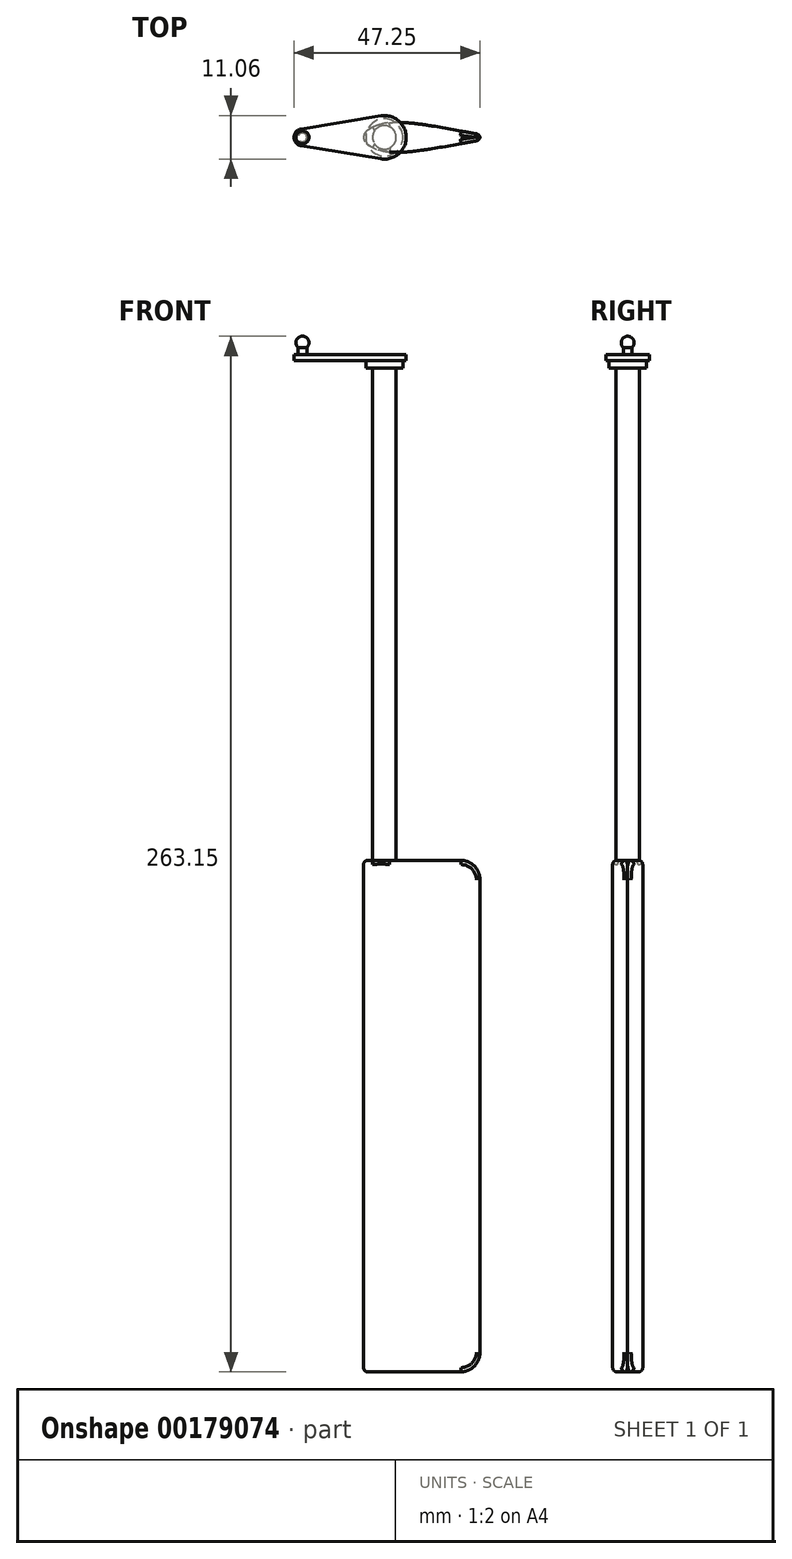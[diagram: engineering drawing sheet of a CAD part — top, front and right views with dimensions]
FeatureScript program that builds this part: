
annotation { "Feature Type Name" : "Feature", "Feature Type Description" : "" }
export const myFeature = defineFeature(function(context is Context, id is Id, definition is map)
    precondition{}
    {
        {
            var Q0;
            Q0=qCreatedBy(makeId("Top.planeOp"),FACE);
            var sketch = newSketch(context, id + "F0", { "sketchPlane" : qUnion([Q0])});
            skCircle(sketch, "E0", {"center": v(0, 0) * mm, "radius": 3 * mm});
            skSolve(sketch);
        }
        {
            var Q0;
            Q0=makeQuery(id+"F0.imprint","IMPRINT",FACE,{"disambiguationData":[TD([[makeQuery(id+"F0.imprint","IMPRINT",EDGE,{"derivedFrom":sQuery(id+"F0.wireOp",EDGE,"E0")}),1.0]])]});
            extrude(context, id + "F1", {"entities" : qUnion([Q0]), "depth" : 125 * mm});
        }
        {
            var Q0;
            Q0=makeQuery(id+"F1.opExtrude","CAP_FACE",FACE,{"disambiguationData":[OSD([sQuery(id+"F0.wireOp",EDGE,"E0")])],"isStart":false});
            var sketch = newSketch(context, id + "F2", { "sketchPlane" : qUnion([Q0])});
            skCircle(sketch, "E1", {"center": v(0, 0) * mm, "radius": 4.7 * mm});
            skSolve(sketch);
        }
        {
            var Q0;
            Q0=makeQuery(id+"F2.imprint","IMPRINT",FACE,{"disambiguationData":[TD([[makeQuery(id+"F2.imprint","IMPRINT",EDGE,{"derivedFrom":sQuery(id+"F2.wireOp",EDGE,"E1")}),1.0]])]});
            var Q1;
            Q1=makeQuery(id+"F2.imprint","IMPRINT",FACE,{"disambiguationData":[TD([[makeQuery(id+"F2.imprint","IMPRINT",EDGE,{"derivedFrom":makeQuery(id+"F1.opExtrude","CAP_EDGE",EDGE,{"disambiguationData":[OSD([sQuery(id+"F0.wireOp",EDGE,"E0")])],"isStart":false})}),1.0]])]});
            extrude(context, id + "F3", {"entities" : qUnion([Q0, Q1]), "operationType" : NewBodyOperationType.ADD, "depth" : 2 * mm});
        }
        {
            var Q0;
            Q0=makeQuery(id+"F3.opExtrude","CAP_FACE",FACE,{"disambiguationData":[OSD([sQuery(id+"F2.wireOp",EDGE,"E1")])],"isStart":false});
            var sketch = newSketch(context, id + "F4", { "sketchPlane" : qUnion([Q0])});
            skArc(sketch, "E2", {"start": v(-0.9, -5.46) * mm, "mid": v(5.53, 0) * mm, "end": v(-0.9, 5.46) * mm});
            skLineSegment(sketch, "E3", {"start": v(0, 0) * mm, "end": v(-20.81, 0) * mm});
            skArc(sketch, "E4", {"start": v(-21.16, 2.12) * mm, "mid": v(-22.97, 0) * mm, "end": v(-21.16, -2.12) * mm});
            skLineSegment(sketch, "E5", {"start": v(-21.16, 2.12) * mm, "end": v(-0.9, 5.46) * mm});
            skLineSegment(sketch, "E6", {"start": v(-21.16, -2.12) * mm, "end": v(-0.9, -5.46) * mm});
            skSolve(sketch);
        }
        {
            var Q0;
            Q0=makeQuery(id+"F4.imprint","IMPRINT",FACE,{"disambiguationData":[TD([[makeQuery(id+"F4.imprint","IMPRINT",EDGE,{"derivedFrom":sQuery(id+"F4.wireOp",EDGE,"E2")}),1.0]])]});
            var Q1;
            Q1=makeQuery(id+"F4.imprint","IMPRINT",FACE,{"disambiguationData":[TD([[makeQuery(id+"F4.imprint","IMPRINT",EDGE,{"derivedFrom":makeQuery(id+"F3.opExtrude","CAP_EDGE",EDGE,{"disambiguationData":[OSD([sQuery(id+"F2.wireOp",EDGE,"E1")])],"isStart":false})}),1.0]])]});
            extrude(context, id + "F5", {"entities" : qUnion([Q0, Q1]), "operationType" : NewBodyOperationType.ADD, "depth" : 1.5 * mm});
        }
        {
            var Q0;
            Q0=makeQuery(id+"F5.opExtrude","CAP_FACE",FACE,{"disambiguationData":[OSD([sQuery(id+"F4.wireOp",EDGE,"E2"),sQuery(id+"F4.wireOp",EDGE,"E4"),sQuery(id+"F4.wireOp",EDGE,"E5"),sQuery(id+"F4.wireOp",EDGE,"E6")])],"isStart":false});
            var sketch = newSketch(context, id + "F6", { "sketchPlane" : qUnion([Q0])});
            skCircle(sketch, "E7", {"center": v(-20.81, 0) * mm, "radius": 1.1 * mm});
            skSolve(sketch);
        }
        {
            var Q0;
            Q0=makeQuery(id+"F6.imprint","IMPRINT",FACE,{"disambiguationData":[TD([[makeQuery(id+"F6.imprint","IMPRINT",EDGE,{"derivedFrom":sQuery(id+"F6.wireOp",EDGE,"E7")}),1.0]])]});
            extrude(context, id + "F7", {"entities" : qUnion([Q0]), "operationType" : NewBodyOperationType.ADD, "depth" : 3 * mm});
        }
        {
            var Q0;
            Q0=makeQuery(id+"F7.opExtrude","CAP_FACE",FACE,{"disambiguationData":[OSD([sQuery(id+"F6.wireOp",EDGE,"E7")])],"isStart":false});
            var sketch = newSketch(context, id + "F8", { "sketchPlane" : qUnion([Q0])});
            skLineSegment(sketch, "E8", {"start": v(-19.17, 0) * mm, "end": v(-22.46, 0) * mm});
            skArc(sketch, "E9", {"start": v(-19.17, 0) * mm, "mid": v(-20.81, 1.65) * mm, "end": v(-22.46, 0) * mm});
            skSolve(sketch);
        }
        {
            var Q0;
            {var subQ0=sQuery(id+"F8.wireOp",EDGE,"E9");Q0=makeQuery(id+"F8.imprint","IMPRINT",FACE,{"disambiguationData":[TD([[makeQuery(id+"F8.imprint","IMPRINT",EDGE,{"derivedFrom":subQ0}),1.0]])]});}
            var Q1;
            {var subQ0=sQuery(id+"F8.wireOp",EDGE,"E8");var subQ1=makeQuery(id+"F7.opExtrude","CAP_EDGE",EDGE,{"disambiguationData":[OSD([sQuery(id+"F6.wireOp",EDGE,"E7")])],"isStart":false});var subQ2=makeQuery(id+"F8.imprint","INTERSECT",VERTEX,{"disambiguationData":[OD(0.0)],"derivedFrom":[subQ1,subQ0]});Q1=makeQuery(id+"F8.imprint","IMPRINT",FACE,{"disambiguationData":[TD([[makeQuery(id+"F8.imprint","IMPRINT",EDGE,{"disambiguationData":[TD([[subQ2,-1.0]])],"derivedFrom":subQ0}),-1.0]])]});}
            var Q2;
            Q2=sQuery(id+"F8.wireOp",EDGE,"E8");
            revolve(context, id + "F9", {"operationType" : NewBodyOperationType.ADD, "entities" : qUnion([Q0, Q1]), "axis" : qUnion([Q2]), "revolveType" : RevolveType.FULL});
        }
        {
            var Q0;
            Q0=makeQuery(id+"F1.opExtrude","CAP_FACE",FACE,{"disambiguationData":[OSD([sQuery(id+"F0.wireOp",EDGE,"E0")])],"isStart":true});
            var sketch = newSketch(context, id + "F10", { "sketchPlane" : qUnion([Q0])});
            skArc(sketch, "E10", {"start": v(3.2, 0) * mm, "mid": v(-1.05, 3.02) * mm, "end": v(-2.51, -1.98) * mm});
            skLineSegment(sketch, "E11", {"start": v(0, 0) * mm, "end": v(24.3, 0) * mm});
            skLineSegment(sketch, "E12", {"start": v(24.3, 0) * mm, "end": v(24.3, 0.73) * mm});
            skLineSegment(sketch, "E13", {"start": v(0, 0) * mm, "end": v(-3.2, 0) * mm});
            skArc(sketch, "E14", {"start": v(-4.54, 1.6) * mm, "mid": v(-5.29, 0) * mm, "end": v(-4.54, -1.6) * mm});
            skFitSpline(sketch, "E15", {"points": [v(24.3, 0.73) * mm, v(2.93, 3.82) * mm, v(-4.54, 1.6) * mm], "startDerivative": vector(-36.88, 6.17) * mm, "endDerivative": vector(-13.95, -11.75) * mm});
            skFitSpline(sketch, "E16.MirrorCS", {"points": [v(24.3, -0.73) * mm, v(2.93, -3.82) * mm, v(-4.54, -1.6) * mm], "startDerivative": vector(-36.88, -6.17) * mm, "endDerivative": vector(-13.95, 11.75) * mm});
            skLineSegment(sketch, "E17.MirrorCS", {"start": v(24.3, 0) * mm, "end": v(24.3, -0.73) * mm});
            skArc(sketch, "E18.trimOffspring", {"start": v(-2.51, -1.98) * mm, "mid": v(-1.1, 0) * mm, "end": v(-2.51, 1.98) * mm});
            skSolve(sketch);
        }
        {
            var Q0;
            Q0=makeQuery(id+"F10.imprint","IMPRINT",FACE,{"disambiguationData":[TD([[makeQuery(id+"F10.imprint","IMPRINT",EDGE,{"derivedFrom":sQuery(id+"F10.wireOp",EDGE,"E12")}),1.0]])]});
            var Q1;
            {var subQ0=sQuery(id+"F10.wireOp",EDGE,"E13");var subQ1=sQuery(id+"F10.wireOp",EDGE,"E11");var subQ2=makeQuery(id+"F10.imprint","INTERSECT",VERTEX,{"derivedFrom":[subQ1,subQ0]});Q1=makeQuery(id+"F10.imprint","IMPRINT",FACE,{"disambiguationData":[TD([[makeQuery(id+"F10.imprint","IMPRINT",EDGE,{"disambiguationData":[TD([[subQ2,-1.0]])],"derivedFrom":subQ1}),1.0]])]});}
            var Q2;
            {var subQ0=sQuery(id+"F10.wireOp",EDGE,"E13");var subQ1=sQuery(id+"F10.wireOp",EDGE,"E11");var subQ2=makeQuery(id+"F10.imprint","INTERSECT",VERTEX,{"derivedFrom":[subQ1,subQ0]});Q2=makeQuery(id+"F10.imprint","IMPRINT",FACE,{"disambiguationData":[TD([[makeQuery(id+"F10.imprint","IMPRINT",EDGE,{"disambiguationData":[TD([[subQ2,-1.0]])],"derivedFrom":subQ1}),-1.0]])]});}
            var Q3;
            {var subQ0=sQuery(id+"F10.wireOp",EDGE,"E18.trimOffspring");var subQ1=sQuery(id+"F10.wireOp",EDGE,"E13");var subQ2=makeQuery(id+"F10.imprint","INTERSECT",VERTEX,{"derivedFrom":[subQ1,subQ0]});Q3=makeQuery(id+"F10.imprint","IMPRINT",FACE,{"disambiguationData":[TD([[makeQuery(id+"F10.imprint","IMPRINT",EDGE,{"disambiguationData":[TD([[subQ2,-1.0]])],"derivedFrom":subQ1}),1.0]])]});}
            var Q4;
            {var subQ0=sQuery(id+"F10.wireOp",EDGE,"E18.trimOffspring");var subQ1=sQuery(id+"F10.wireOp",EDGE,"E13");var subQ2=makeQuery(id+"F10.imprint","INTERSECT",VERTEX,{"derivedFrom":[subQ1,subQ0]});Q4=makeQuery(id+"F10.imprint","IMPRINT",FACE,{"disambiguationData":[TD([[makeQuery(id+"F10.imprint","IMPRINT",EDGE,{"disambiguationData":[TD([[subQ2,-1.0]])],"derivedFrom":subQ1}),-1.0]])]});}
            var Q5;
            {var subQ0=sQuery(id+"F10.wireOp",EDGE,"E11");var subQ1=sQuery(id+"F10.wireOp",EDGE,"E10");var subQ2=makeQuery(id+"F10.imprint","INTERSECT",VERTEX,{"derivedFrom":[subQ1,subQ0]});Q5=makeQuery(id+"F10.imprint","IMPRINT",FACE,{"disambiguationData":[TD([[makeQuery(id+"F10.imprint","IMPRINT",EDGE,{"disambiguationData":[TD([[subQ2,-1.0]])],"derivedFrom":subQ1}),1.0]])]});}
            var Q6;
            {var subQ0=sQuery(id+"F10.wireOp",EDGE,"E13");var subQ1=sQuery(id+"F10.wireOp",EDGE,"E10");var subQ2=makeQuery(id+"F10.imprint","INTERSECT",VERTEX,{"derivedFrom":[subQ1,subQ0]});Q6=makeQuery(id+"F10.imprint","IMPRINT",FACE,{"disambiguationData":[TD([[makeQuery(id+"F10.imprint","IMPRINT",EDGE,{"disambiguationData":[TD([[subQ2,1.0]])],"derivedFrom":subQ1}),1.0]])]});}
            var Q7;
            {var subQ0=sQuery(id+"F10.wireOp",EDGE,"E18.trimOffspring");var subQ1=sQuery(id+"F10.wireOp",EDGE,"E10");var subQ2=makeQuery(id+"F10.imprint","INTERSECT",VERTEX,{"disambiguationData":[OD(0.0)],"derivedFrom":[subQ1,subQ0]});Q7=makeQuery(id+"F10.imprint","IMPRINT",FACE,{"disambiguationData":[TD([[makeQuery(id+"F10.imprint","IMPRINT",EDGE,{"disambiguationData":[TD([[subQ2,1.0]])],"derivedFrom":subQ1}),1.0]])]});}
            extrude(context, id + "F11", {"entities" : qUnion([Q0, Q1, Q2, Q3, Q4, Q5, Q6, Q7]), "operationType" : NewBodyOperationType.ADD, "depth" : 130 * mm});
        }
        {
            var Q0;
            Q0=makeQuery(id+"F11.opExtrude","CAP_EDGE",EDGE,{"disambiguationData":[OSD([sQuery(id+"F10.wireOp",EDGE,"E12"),sQuery(id+"F10.wireOp",EDGE,"E17.MirrorCS")])],"isStart":true});
            fillet(context, id + "F12", {"entities" : qUnion([Q0]), "radius" : 5 * mm, "tangentPropagation" : true, "allowEdgeOverflow" : false});
        }
        {
            var Q0;
            Q0=makeQuery(id+"F11.opExtrude","CAP_EDGE",EDGE,{"disambiguationData":[OSD([sQuery(id+"F10.wireOp",EDGE,"E12"),sQuery(id+"F10.wireOp",EDGE,"E17.MirrorCS")])],"isStart":false});
            fillet(context, id + "F13", {"entities" : qUnion([Q0]), "radius" : 5 * mm, "tangentPropagation" : true, "allowEdgeOverflow" : false});
        }
        {
            var Q0;
            Q0=makeQuery(id+"F11.opExtrude","CAP_EDGE",EDGE,{"disambiguationData":[OSD([sQuery(id+"F10.wireOp",EDGE,"E15")])],"isStart":true});
            fillet(context, id + "F14", {"entities" : qUnion([Q0]), "radius" : 1.1 * mm, "tangentPropagation" : true, "allowEdgeOverflow" : false});
        }
    });
